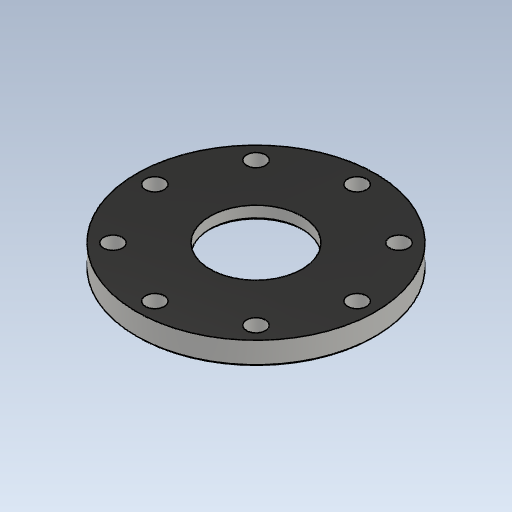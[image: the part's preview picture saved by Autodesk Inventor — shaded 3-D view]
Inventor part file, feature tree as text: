
AUTODESK INVENTOR PART (.ipt)
format: ipt  version: 2023 (Build 270158000, 158)  size: 359,936 bytes
history: native  units: mm
features: other x2, extrude x2, sketch x1, imported_body x1
ambient origin geometry x8: Origin, YZ Plane, XZ Plane, XY Plane, X Axis, Y Axis, Z Axis, Center Point
bodies: Body1 (feature_tree)
feature tree (6):
  other  "ソリッド1"
  other  "作業平面1"
  extrude  "押し出し1"  Depth=1.0mm
  extrude  "押し出し2"  Depth=10.0mm TaperAngle=0.0deg
  sketch  "スケッチ1"
  imported_body  "Base1"
